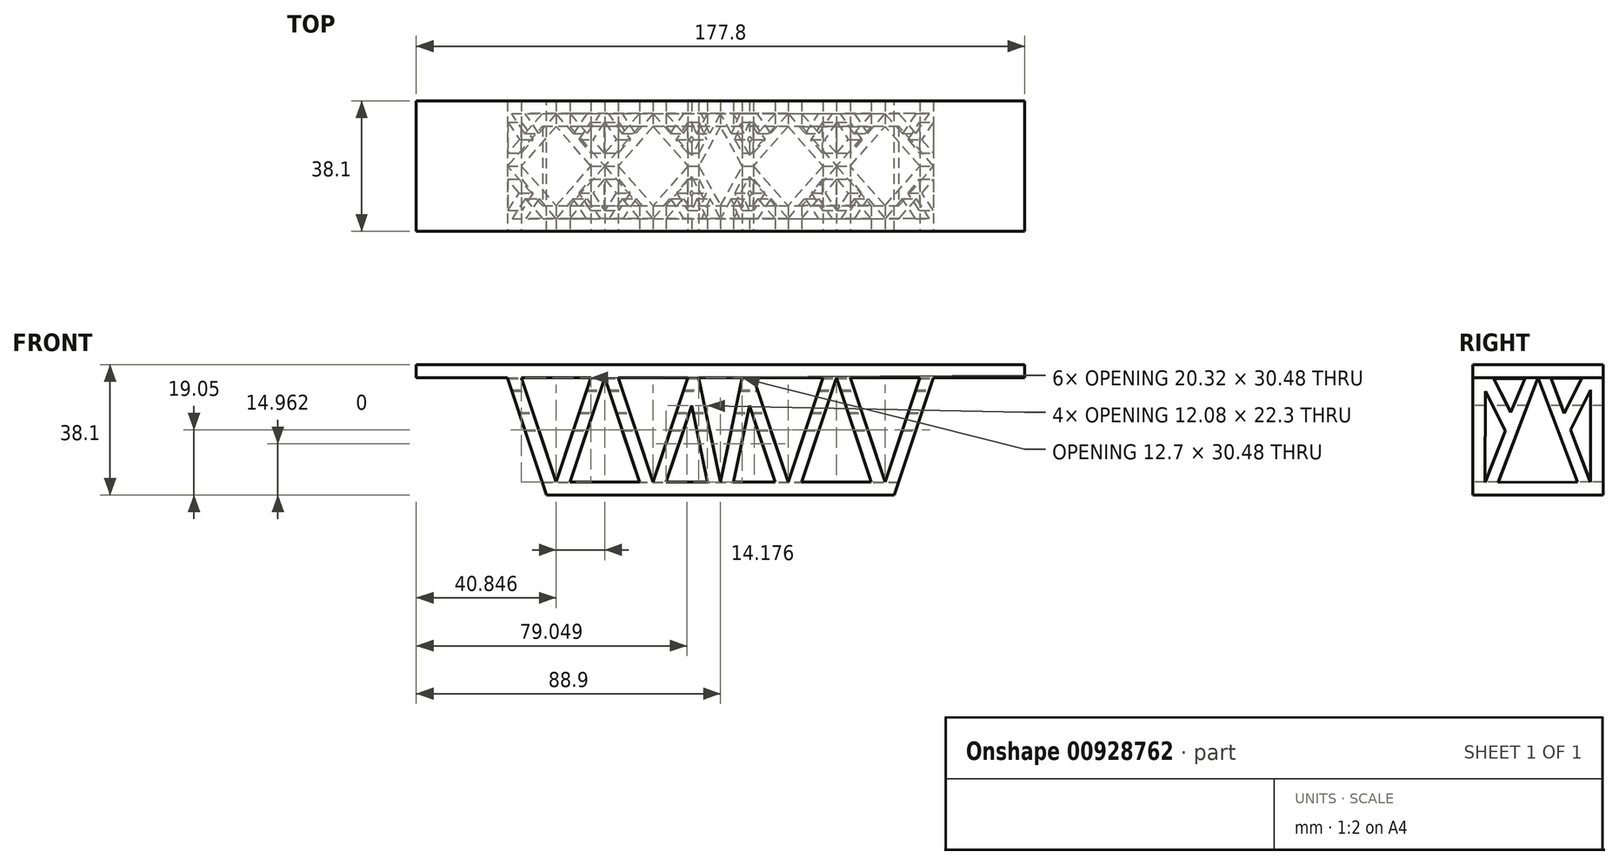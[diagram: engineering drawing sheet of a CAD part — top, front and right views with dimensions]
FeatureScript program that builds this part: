
annotation { "Feature Type Name" : "Feature", "Feature Type Description" : "" }
export const myFeature = defineFeature(function(context is Context, id is Id, definition is map)
    precondition{}
    {
        {
            var Q0;
            Q0=qCreatedBy(makeId("Front.planeOp"),FACE);
            var sketch = newSketch(context, id + "F0", { "sketchPlane" : qUnion([Q0])});
            skLineSegment(sketch, "E0.bottom", {"start": v(-88.9, 38.1) * mm, "end": v(88.9, 38.1) * mm, "construction": true});
            skLineSegment(sketch, "E0.top", {"start": v(-88.9, -38.1) * mm, "end": v(88.9, -38.1) * mm, "construction": true});
            skLineSegment(sketch, "E0.left", {"start": v(-88.9, 38.1) * mm, "end": v(-88.9, -38.1) * mm, "construction": true});
            skLineSegment(sketch, "E0.right", {"start": v(88.9, 38.1) * mm, "end": v(88.9, -38.1) * mm, "construction": true});
            skPoint(sketch, "E0.middle", {"position": v(0, 0) * mm});
            skLineSegment(sketch, "E1", {"start": v(-88.9, -38.1) * mm, "end": v(-63.5, -38.1) * mm, "construction": true});
            skLineSegment(sketch, "E2", {"start": v(88.9, -38.1) * mm, "end": v(63.5, -38.1) * mm, "construction": true});
            skLineSegment(sketch, "E3", {"start": v(-63.5, -38.1) * mm, "end": v(-63.5, 38.1) * mm, "construction": true});
            skLineSegment(sketch, "E4", {"start": v(63.5, -38.1) * mm, "end": v(63.5, 38.1) * mm, "construction": true});
            skLineSegment(sketch, "E5", {"start": v(63.5, 38.1) * mm, "end": v(-63.5, 38.1) * mm, "construction": true});
            skLineSegment(sketch, "E6", {"start": v(-63.5, 0) * mm, "end": v(63.5, 0) * mm});
            skLineSegment(sketch, "E7", {"start": v(-50.8, -38.1) * mm, "end": v(50.8, -38.1) * mm});
            skLineSegment(sketch, "E8", {"start": v(-63.5, 0) * mm, "end": v(-50.8, -38.1) * mm});
            skLineSegment(sketch, "E9", {"start": v(63.5, 0) * mm, "end": v(50.8, -38.1) * mm});
            skSolve(sketch);
        }
        {
            var Q0;
            Q0=makeQuery(id+"F0.imprint","IMPRINT",FACE,{"disambiguationData":[TD([[makeQuery(id+"F0.imprint","IMPRINT",EDGE,{"derivedFrom":sQuery(id+"F0.wireOp",EDGE,"E6")}),-1.0]])]});
            extrude(context, id + "F1", {"entities" : qUnion([Q0]), "endBound" : BoundingType.SYMMETRIC, "depth" : 38.1 * mm, "offsetDistance" : 25.4 * mm});
        }
        {
            var Q0;
            Q0=qCreatedBy(makeId("Right.planeOp"),FACE);
            var sketch = newSketch(context, id + "F2", { "sketchPlane" : qUnion([Q0])});
            skLineSegment(sketch, "E10", {"start": v(15.08, -4) * mm, "end": v(8.23, -17.6) * mm, "construction": true});
            skLineSegment(sketch, "E11", {"start": v(-15.13, -4) * mm, "end": v(-8.28, -17.6) * mm, "construction": true});
            skLineSegment(sketch, "E12", {"start": v(-8.28, -17.6) * mm, "end": v(8.23, -17.6) * mm, "construction": true});
            skLineSegment(sketch, "E13", {"start": v(17.12, -3.95) * mm, "end": v(9.36, -19.38) * mm});
            skLineSegment(sketch, "E14", {"start": v(9.36, -19.38) * mm, "end": v(5.95, -17.67) * mm});
            skLineSegment(sketch, "E15", {"start": v(5.95, -17.67) * mm, "end": v(13.72, -2.24) * mm});
            skLineSegment(sketch, "E16", {"start": v(13.72, -2.24) * mm, "end": v(17.12, -3.95) * mm});
            skLineSegment(sketch, "E17", {"start": v(-17.2, -4) * mm, "end": v(-9.44, -19.42) * mm});
            skLineSegment(sketch, "E18", {"start": v(-9.44, -19.42) * mm, "end": v(-6.09, -17.6) * mm});
            skLineSegment(sketch, "E19", {"start": v(-6.09, -17.6) * mm, "end": v(-13.85, -2.18) * mm});
            skLineSegment(sketch, "E20", {"start": v(-13.85, -2.18) * mm, "end": v(-17.2, -4) * mm});
            skSolve(sketch);
        }
        {
            var Q0;
            Q0=makeQuery(id+"F2.imprint","IMPRINT",FACE,{"disambiguationData":[TD([[makeQuery(id+"F2.imprint","IMPRINT",EDGE,{"derivedFrom":sQuery(id+"F2.wireOp",EDGE,"E17")}),1.0]])]});
            var Q1;
            Q1=makeQuery(id+"F2.imprint","IMPRINT",FACE,{"disambiguationData":[TD([[makeQuery(id+"F2.imprint","IMPRINT",EDGE,{"derivedFrom":sQuery(id+"F2.wireOp",EDGE,"E13")}),-1.0]])]});
            extrude(context, id + "F3", {"entities" : qUnion([Q0, Q1]), "operationType" : NewBodyOperationType.ADD, "endBound" : BoundingType.SYMMETRIC, "depth" : 129.54 * mm, "offsetDistance" : 25.4 * mm});
        }
        {
            var Q0;
            Q0=makeQuery(id+"F1.opExtrude","CAP_FACE",FACE,{"disambiguationData":[OSD([sQuery(id+"F0.wireOp",EDGE,"E6"),sQuery(id+"F0.wireOp",EDGE,"E7"),sQuery(id+"F0.wireOp",EDGE,"E8"),sQuery(id+"F0.wireOp",EDGE,"E9")])],"isStart":false});
            var sketch = newSketch(context, id + "F4", { "sketchPlane" : qUnion([Q0])});
            skLineSegment(sketch, "E21.1", {"start": v(-58.21, -3.8) * mm, "end": v(-48.05, -34.29) * mm, "construction": true});
            skLineSegment(sketch, "E21.3", {"start": v(58.21, -3.8) * mm, "end": v(48.05, -34.29) * mm, "construction": true});
            skLineSegment(sketch, "E22", {"start": v(-58.21, -3.8) * mm, "end": v(-48.05, -34.29) * mm});
            skLineSegment(sketch, "E23", {"start": v(-48.05, -34.29) * mm, "end": v(-37.9, -3.8) * mm});
            skLineSegment(sketch, "E24", {"start": v(48.05, -34.29) * mm, "end": v(37.9, -3.8) * mm});
            skLineSegment(sketch, "E25", {"start": v(48.05, -34.29) * mm, "end": v(58.21, -3.8) * mm});
            skLineSegment(sketch, "E26", {"start": v(-58.21, -3.8) * mm, "end": v(-37.9, -3.8) * mm});
            skLineSegment(sketch, "E27", {"start": v(37.9, -3.8) * mm, "end": v(58.21, -3.8) * mm});
            skLineSegment(sketch, "E28", {"start": v(-33.88, -3.8) * mm, "end": v(-44.04, -34.29) * mm});
            skLineSegment(sketch, "E29", {"start": v(33.88, -3.8) * mm, "end": v(44.04, -34.29) * mm});
            skLineSegment(sketch, "E30", {"start": v(-44.04, -34.29) * mm, "end": v(-23.72, -34.29) * mm});
            skLineSegment(sketch, "E31", {"start": v(44.04, -34.29) * mm, "end": v(23.72, -34.29) * mm});
            skLineSegment(sketch, "E32", {"start": v(-33.88, -3.8) * mm, "end": v(-23.72, -34.29) * mm});
            skLineSegment(sketch, "E33", {"start": v(33.88, -3.8) * mm, "end": v(23.72, -34.3) * mm});
            skLineSegment(sketch, "E34", {"start": v(-29.86, -3.8) * mm, "end": v(-19.7, -34.29) * mm});
            skLineSegment(sketch, "E35", {"start": v(29.86, -3.8) * mm, "end": v(19.7, -34.29) * mm});
            skLineSegment(sketch, "E36", {"start": v(-29.86, -3.8) * mm, "end": v(-9.54, -3.8) * mm});
            skLineSegment(sketch, "E37", {"start": v(29.86, -3.8) * mm, "end": v(9.54, -3.8) * mm});
            skLineSegment(sketch, "E38", {"start": v(-9.54, -3.8) * mm, "end": v(-19.7, -34.29) * mm});
            skLineSegment(sketch, "E39", {"start": v(9.54, -3.8) * mm, "end": v(19.7, -34.29) * mm});
            skLineSegment(sketch, "E40", {"start": v(-48.05, -34.29) * mm, "end": v(48.05, -34.29) * mm, "construction": true});
            skLineSegment(sketch, "E41", {"start": v(-58.21, -3.8) * mm, "end": v(58.21, -3.8) * mm, "construction": true});
            skLineSegment(sketch, "E42", {"start": v(0, 0) * mm, "end": v(0, -3.8) * mm});
            skLineSegment(sketch, "E43", {"start": v(0, -3.8) * mm, "end": v(6.35, -3.8) * mm});
            skLineSegment(sketch, "E44", {"start": v(0, -3.8) * mm, "end": v(-6.35, -3.8) * mm});
            skLineSegment(sketch, "E45", {"start": v(-6.35, -3.8) * mm, "end": v(0, -34.29) * mm});
            skLineSegment(sketch, "E46", {"start": v(0, -34.29) * mm, "end": v(6.35, -3.8) * mm});
            skLineSegment(sketch, "E47", {"start": v(3.81, -34.29) * mm, "end": v(15.9, -34.29) * mm});
            skLineSegment(sketch, "E48", {"start": v(-15.9, -34.29) * mm, "end": v(-3.8, -34.29) * mm});
            skPoint(sketch, "E49.endSnap0", {"position": v(9.85, -34.29) * mm});
            skLineSegment(sketch, "E50", {"start": v(-8.46, -11.99) * mm, "end": v(-15.9, -34.29) * mm});
            skLineSegment(sketch, "E51", {"start": v(-8.46, -11.99) * mm, "end": v(-3.8, -34.29) * mm});
            skLineSegment(sketch, "E52", {"start": v(3.81, -34.29) * mm, "end": v(8.46, -11.99) * mm});
            skLineSegment(sketch, "E53", {"start": v(8.46, -11.99) * mm, "end": v(15.9, -34.29) * mm});
            skSolve(sketch);
        }
        {
            var Q0;
            Q0=makeQuery(id+"F4.imprint","IMPRINT",FACE,{"disambiguationData":[TD([[makeQuery(id+"F4.imprint","IMPRINT",EDGE,{"derivedFrom":sQuery(id+"F4.wireOp",EDGE,"E35")}),-1.0]])]});
            var Q1;
            Q1=makeQuery(id+"F4.imprint","IMPRINT",FACE,{"disambiguationData":[TD([[makeQuery(id+"F4.imprint","IMPRINT",EDGE,{"derivedFrom":sQuery(id+"F4.wireOp",EDGE,"E29")}),-1.0]])]});
            var Q2;
            Q2=makeQuery(id+"F4.imprint","IMPRINT",FACE,{"disambiguationData":[TD([[makeQuery(id+"F4.imprint","IMPRINT",EDGE,{"derivedFrom":sQuery(id+"F4.wireOp",EDGE,"E24")}),-1.0]])]});
            var Q3;
            Q3=makeQuery(id+"F4.imprint","IMPRINT",FACE,{"disambiguationData":[TD([[makeQuery(id+"F4.imprint","IMPRINT",EDGE,{"derivedFrom":sQuery(id+"F4.wireOp",EDGE,"E34")}),1.0]])]});
            var Q4;
            Q4=makeQuery(id+"F4.imprint","IMPRINT",FACE,{"disambiguationData":[TD([[makeQuery(id+"F4.imprint","IMPRINT",EDGE,{"derivedFrom":sQuery(id+"F4.wireOp",EDGE,"E28")}),1.0]])]});
            var Q5;
            Q5=makeQuery(id+"F4.imprint","IMPRINT",FACE,{"disambiguationData":[TD([[makeQuery(id+"F4.imprint","IMPRINT",EDGE,{"derivedFrom":sQuery(id+"F4.wireOp",EDGE,"E22")}),1.0]])]});
            var Q6;
            Q6=makeQuery(id+"F4.imprint","IMPRINT",FACE,{"disambiguationData":[TD([[makeQuery(id+"F4.imprint","IMPRINT",EDGE,{"derivedFrom":sQuery(id+"F4.wireOp",EDGE,"fIM3GQ1g-4FJD-daXr-pOhc-P1qinkdojLdS")}),1.0]])]});
            var Q7;
            Q7=makeQuery(id+"F4.imprint","IMPRINT",FACE,{"disambiguationData":[TD([[makeQuery(id+"F4.imprint","IMPRINT",EDGE,{"derivedFrom":sQuery(id+"F4.wireOp",EDGE,"m0uD7bOc-jWjE-plLZ-odWu-XJtLTIfpsfuD")}),-1.0]])]});
            var Q8;
            Q8=makeQuery(id+"F4.imprint","IMPRINT",FACE,{"disambiguationData":[TD([[makeQuery(id+"F4.imprint","IMPRINT",EDGE,{"derivedFrom":sQuery(id+"F4.wireOp",EDGE,"eOtnskWI-COLx-ZRnQ-VyK4-OVioc3qGVgg9")}),-1.0]])]});
            var Q9;
            {var subQ2=sQuery(id+"F4.wireOp",EDGE,"bDtsqGfJ-kTeU-ICjX-jhcc-96lbrGubuKwS");Q9=makeQuery(id+"F4.imprint","IMPRINT",FACE,{"disambiguationData":[TD([[makeQuery(id+"F4.imprint","IMPRINT",EDGE,{"derivedFrom":subQ2}),1.0]])]});}
            var Q10;
            Q10=makeQuery(id+"F4.imprint","IMPRINT",FACE,{"disambiguationData":[TD([[makeQuery(id+"F4.imprint","IMPRINT",EDGE,{"derivedFrom":sQuery(id+"F4.wireOp",EDGE,"Sd1ywjxl-7Lnk-4QA6-EBgl-iMDLKzbaIvO9")}),1.0]])]});
            var Q11;
            {var subQ2=sQuery(id+"F4.wireOp",EDGE,"JuoAtM5F-oohW-8M1N-ToQ0-xAbWZhJYV4DC");Q11=makeQuery(id+"F4.imprint","IMPRINT",FACE,{"disambiguationData":[TD([[makeQuery(id+"F4.imprint","IMPRINT",EDGE,{"derivedFrom":subQ2}),-1.0]])]});}
            var Q12;
            Q12=makeQuery(id+"F4.imprint","IMPRINT",FACE,{"disambiguationData":[TD([[makeQuery(id+"F4.imprint","IMPRINT",EDGE,{"derivedFrom":sQuery(id+"F4.wireOp",EDGE,"E48")}),1.0]])]});
            var Q13;
            Q13=makeQuery(id+"F4.imprint","IMPRINT",FACE,{"disambiguationData":[TD([[makeQuery(id+"F4.imprint","IMPRINT",EDGE,{"derivedFrom":sQuery(id+"F4.wireOp",EDGE,"E43")}),-1.0]])]});
            var Q14;
            Q14=makeQuery(id+"F4.imprint","IMPRINT",FACE,{"disambiguationData":[TD([[makeQuery(id+"F4.imprint","IMPRINT",EDGE,{"derivedFrom":sQuery(id+"F4.wireOp",EDGE,"E47")}),1.0]])]});
            extrude(context, id + "F5", {"entities" : qUnion([Q0, Q1, Q2, Q3, Q4, Q5, Q6, Q7, Q8, Q9, Q10, Q11, Q12, Q13, Q14]), "operationType" : NewBodyOperationType.REMOVE, "endBound" : BoundingType.THROUGH_ALL, "oppositeDirection" : true, "depth" : 25.4 * mm, "offsetDistance" : 25.4 * mm});
        }
        {
            var Q0;
            Q0=qCreatedBy(makeId("Right.planeOp"),FACE);
            var sketch = newSketch(context, id + "F6", { "sketchPlane" : qUnion([Q0])});
            skLineSegment(sketch, "E54", {"start": v(0, -3.8) * mm, "end": v(11.63, -34.32) * mm});
            skLineSegment(sketch, "E55", {"start": v(11.63, -34.32) * mm, "end": v(-11.6, -34.36) * mm});
            skLineSegment(sketch, "E56", {"start": v(-11.6, -34.36) * mm, "end": v(0, -3.8) * mm});
            skLineSegment(sketch, "E57", {"start": v(12.85, -3.96) * mm, "end": v(3.8, -3.96) * mm});
            skLineSegment(sketch, "E58", {"start": v(7.7, -14.19) * mm, "end": v(12.85, -3.96) * mm});
            skLineSegment(sketch, "E59", {"start": v(15.42, -7.33) * mm, "end": v(9.52, -19.05) * mm});
            skLineSegment(sketch, "E60", {"start": v(15.42, -7.33) * mm, "end": v(15.34, -34.32) * mm});
            skLineSegment(sketch, "E61", {"start": v(-3.8, -4.02) * mm, "end": v(-12.93, -4.02) * mm});
            skLineSegment(sketch, "E62", {"start": v(-12.93, -4.02) * mm, "end": v(-7.93, -13.95) * mm});
            skLineSegment(sketch, "E63", {"start": v(-7.93, -13.95) * mm, "end": v(-3.8, -4.02) * mm});
            skLineSegment(sketch, "E64", {"start": v(-15.34, -7.7) * mm, "end": v(-9.48, -19.34) * mm});
            skLineSegment(sketch, "E65", {"start": v(-9.48, -19.34) * mm, "end": v(-15.42, -34.36) * mm});
            skLineSegment(sketch, "E66", {"start": v(-15.34, -7.7) * mm, "end": v(-15.42, -34.36) * mm});
            skLineSegment(sketch, "E67", {"start": v(9.52, -19.05) * mm, "end": v(15.34, -34.32) * mm});
            skLineSegment(sketch, "E68", {"start": v(7.7, -14.19) * mm, "end": v(3.8, -3.96) * mm});
            skSolve(sketch);
        }
        {
            var Q0;
            Q0 = qSketchRegion(id + "F6", true);
            extrude(context, id + "F7", {"entities" : qUnion([Q0]), "operationType" : NewBodyOperationType.REMOVE, "endBound" : BoundingType.SYMMETRIC, "oppositeDirection" : true, "depth" : 143.26 * mm, "offsetDistance" : 25.4 * mm});
        }
        {
            var Q0;
            Q0=qCreatedBy(makeId("Front.planeOp"),FACE);
            var sketch = newSketch(context, id + "F8", { "sketchPlane" : qUnion([Q0])});
            skLineSegment(sketch, "E69", {"start": v(-63.5, 0) * mm, "end": v(-50.99, -37.54) * mm});
            skLineSegment(sketch, "E70", {"start": v(-50.99, -37.54) * mm, "end": v(-69.82, -37.54) * mm});
            skLineSegment(sketch, "E71", {"start": v(-69.82, -37.54) * mm, "end": v(-69.82, 0) * mm});
            skLineSegment(sketch, "E72", {"start": v(-69.82, 0) * mm, "end": v(-63.5, 0) * mm});
            skLineSegment(sketch, "E73", {"start": v(63.5, 0) * mm, "end": v(50.7, -38.4) * mm});
            skLineSegment(sketch, "E74", {"start": v(50.7, -38.4) * mm, "end": v(71.1, -38.4) * mm});
            skLineSegment(sketch, "E75", {"start": v(71.1, -38.4) * mm, "end": v(71.1, 0) * mm});
            skLineSegment(sketch, "E76", {"start": v(71.1, 0) * mm, "end": v(63.5, 0) * mm});
            skSolve(sketch);
        }
        {
            var Q0;
            Q0=makeQuery(id+"F8.imprint","IMPRINT",FACE,{"disambiguationData":[TD([[makeQuery(id+"F8.imprint","IMPRINT",EDGE,{"derivedFrom":sQuery(id+"F8.wireOp",EDGE,"E73")}),1.0]])]});
            var Q1;
            Q1=makeQuery(id+"F8.imprint","IMPRINT",FACE,{"disambiguationData":[TD([[makeQuery(id+"F8.imprint","IMPRINT",EDGE,{"derivedFrom":sQuery(id+"F8.wireOp",EDGE,"E69")}),-1.0]])]});
            extrude(context, id + "F9", {"entities" : qUnion([Q0, Q1]), "operationType" : NewBodyOperationType.REMOVE, "endBound" : BoundingType.SYMMETRIC, "oppositeDirection" : true, "depth" : 127 * mm, "offsetDistance" : 25.4 * mm});
        }
        {
            var Q0;
            Q0=qCreatedBy(makeId("Front.planeOp"),FACE);
            var sketch = newSketch(context, id + "F10", { "sketchPlane" : qUnion([Q0])});
            skLineSegment(sketch, "E77", {"start": v(-88.9, 0) * mm, "end": v(88.9, 0) * mm});
            skLineSegment(sketch, "E78", {"start": v(-88.9, -3.8) * mm, "end": v(88.9, -3.8) * mm});
            skLineSegment(sketch, "E79", {"start": v(-88.9, 0) * mm, "end": v(-88.9, -3.8) * mm});
            skLineSegment(sketch, "E80", {"start": v(88.9, -3.8) * mm, "end": v(88.9, 0) * mm});
            skSolve(sketch);
        }
        {
            var Q0;
            Q0=makeQuery(id+"F10.imprint","IMPRINT",FACE,{"disambiguationData":[TD([[makeQuery(id+"F10.imprint","IMPRINT",EDGE,{"derivedFrom":sQuery(id+"F10.wireOp",EDGE,"E77")}),-1.0]])]});
            extrude(context, id + "F11", {"entities" : qUnion([Q0]), "operationType" : NewBodyOperationType.ADD, "endBound" : BoundingType.SYMMETRIC, "depth" : 38.1 * mm, "offsetDistance" : 25.4 * mm});
        }
    });
